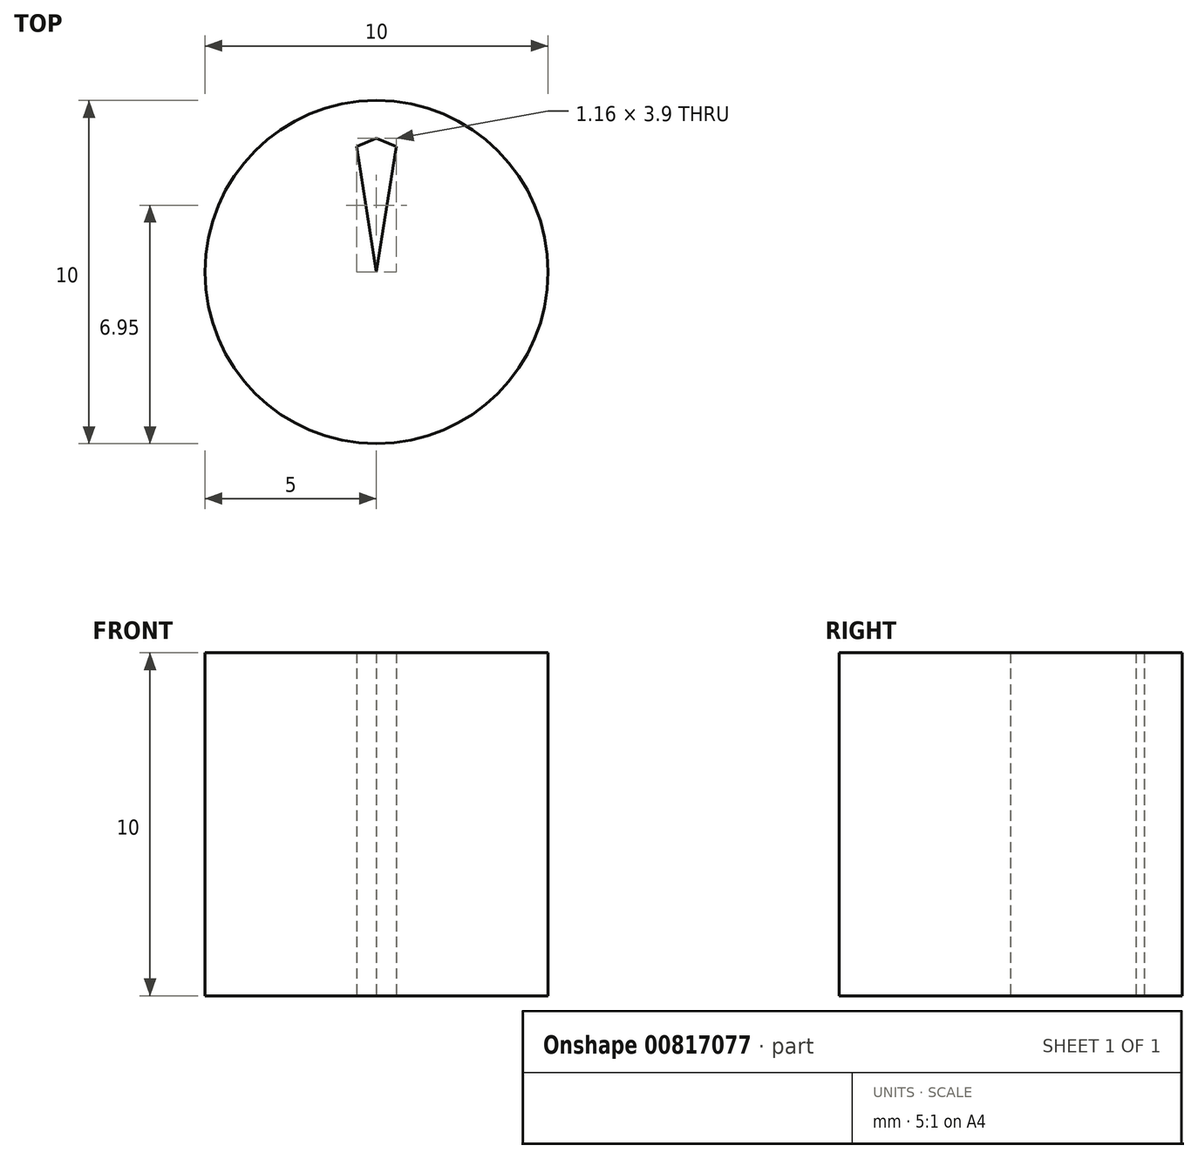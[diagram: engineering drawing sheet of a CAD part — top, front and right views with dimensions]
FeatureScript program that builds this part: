
annotation { "Feature Type Name" : "Feature", "Feature Type Description" : "" }
export const myFeature = defineFeature(function(context is Context, id is Id, definition is map)
    precondition{}
    {
        {
            var Q0;
            Q0=qCreatedBy(makeId("Top.planeOp"),FACE);
            var sketch = newSketch(context, id + "F0", { "sketchPlane" : qUnion([Q0])});
            skCircle(sketch, "E0", {"center": v(0, 0) * mm, "radius": 3.9 * mm, "construction": true});
            skCircle(sketch, "E1", {"center": v(0, 0) * mm, "radius": 3.7 * mm, "construction": true});
            skLineSegment(sketch, "E2", {"start": v(0, 0) * mm, "end": v(-0.7, 4.42) * mm, "construction": true});
            skLineSegment(sketch, "E3", {"start": v(0, 0) * mm, "end": v(0.7, 4.48) * mm, "construction": true});
            skCircle(sketch, "E4", {"center": v(0, 0) * mm, "radius": 5 * mm});
            skLineSegment(sketch, "E5", {"start": v(0, 0) * mm, "end": v(-0.58, 3.65) * mm});
            skLineSegment(sketch, "E6", {"start": v(-0.58, 3.65) * mm, "end": v(0, 3.9) * mm});
            skLineSegment(sketch, "E7", {"start": v(0, 3.9) * mm, "end": v(0.58, 3.65) * mm});
            skLineSegment(sketch, "E8", {"start": v(0.58, 3.65) * mm, "end": v(0, 0) * mm});
            skSolve(sketch);
        }
        {
            var Q0;
            Q0=makeQuery(id+"F0.imprint","IMPRINT",FACE,{"disambiguationData":[TD([[makeQuery(id+"F0.imprint","IMPRINT",EDGE,{"derivedFrom":sQuery(id+"F0.wireOp",EDGE,"E4")}),1.0]])]});
            extrude(context, id + "F1", {"entities" : qUnion([Q0]), "depth" : 10 * mm, "offsetDistance" : 25 * mm});
        }
    });
